# Revit family: Faucet-Lavatory-KOHLER-Aleo-K-29006T_1
name_source: partatom
category: Plumbing Fixtures
units: mm (PartAtom-declared; Revit-internal decimal feet)

## family parameters
Cut with Voids When Loaded = No
Host = Face
OmniClass Number = 23.31.11.00
OmniClass Title = Faucets
Part Type = Normal
Room Calculation Point = No
Round Connector Dimension = Use Diameter
Shared = No

## types (2) — shared parameters
ADA Compliant = No
Assembly Code = D2010
CW Connection = Yes
Cold Water Inlet = Cold Water Inlet
Date Modified = 11/11/2022
Default Elevation = 36"
Description = Induction washbasin faucet (smart model)
Drain Included = No
Faucet Hole Spacing = 0"
Flow Rate = 2 GPM
HW Connection = Yes
Handle Clearance = 3 7/16"
Height = 9 11/16"
Hot Water Inlet = Hot Water Inlet
Length = 5 13/16"
Manufacturer = Kohler Co.
Master Format 2014 = 22 41 39
Master Format 2014 Name = Residential Faucets, Supplies, and Trim
Material = Premium Metal Construction
Pressure = 60.00 psi
Product Documentation Link = https://files.kohler.com.cn
Product Name = Aleo
Product Page URL = https://www.kohler.com.cn
Spout Reach = 5 13/16"
URL = http://www.kohler.com.cn
Vent Connection = No
Waste Connection = No
Waste Water Outlet = Waste Water Outlet
WaterSense Certified = No
Width = 1 7/8"

## per-type parameters (varying)
| type | Finish | Model | Type |
| CP-Polished Chrome | Kohler-Metal-CP-Polished_Chrome | K-29006T-4-CP | 1 |
| ECP-Polished Chrome Plating | KOHLER-Metal-ECP-Polished_Chrome_Plating | K-29006T-4-ECP | 2 |

## geometry (parser evidence)
native form markers: Sweep x4
no freeform markers — native parametric forms only
